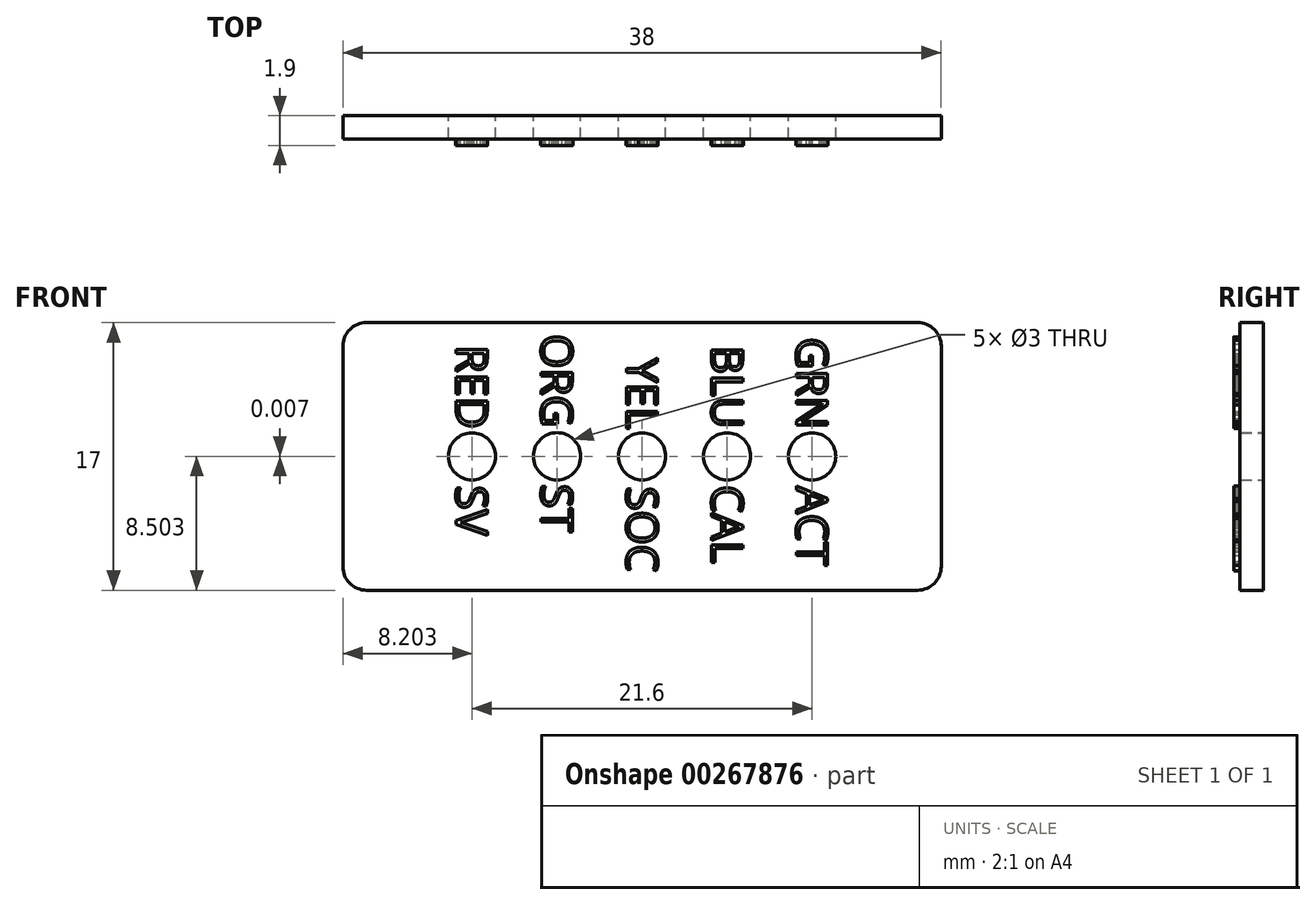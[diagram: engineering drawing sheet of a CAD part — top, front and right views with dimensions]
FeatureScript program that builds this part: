
annotation { "Feature Type Name" : "Feature", "Feature Type Description" : "" }
export const myFeature = defineFeature(function(context is Context, id is Id, definition is map)
    precondition{}
    {
        {
            var Q0;
            Q0=qCreatedBy(makeId("Front.planeOp"),FACE);
            var sketch = newSketch(context, id + "F0", { "sketchPlane" : qUnion([Q0])});
            skLineSegment(sketch, "E0.bottom", {"start": v(-88.73, 33.86) * mm, "end": v(-53.73, 33.86) * mm});
            skLineSegment(sketch, "E0.top", {"start": v(-88.73, 16.86) * mm, "end": v(-53.73, 16.86) * mm});
            skLineSegment(sketch, "E0.left", {"start": v(-90.23, 32.36) * mm, "end": v(-90.23, 18.36) * mm});
            skLineSegment(sketch, "E0.right", {"start": v(-52.23, 32.36) * mm, "end": v(-52.23, 18.36) * mm});
            skLineSegment(sketch, "E1", {"start": v(-94.23, 25.36) * mm, "end": v(-40.36, 25.36) * mm, "construction": true});
            skCircle(sketch, "E2", {"center": v(-82.03, 25.36) * mm, "radius": 1.5 * mm});
            skCircle(sketch, "E3", {"center": v(-76.63, 25.37) * mm, "radius": 1.5 * mm});
            skCircle(sketch, "E4", {"center": v(-71.23, 25.36) * mm, "radius": 1.5 * mm});
            skCircle(sketch, "E5", {"center": v(-65.83, 25.36) * mm, "radius": 1.5 * mm});
            skCircle(sketch, "E6", {"center": v(-60.43, 25.36) * mm, "radius": 1.5 * mm});
            skPoint(sketch, "E7.visualSharp", {"position": v(-90.23, 33.86) * mm});
            skArc(sketch, "E7.filletArc", {"start": v(-88.73, 33.86) * mm, "mid": v(-89.79, 33.42) * mm, "end": v(-90.23, 32.36) * mm});
            skPoint(sketch, "E8.visualSharp", {"position": v(-52.23, 33.86) * mm});
            skArc(sketch, "E8.filletArc", {"start": v(-52.23, 32.36) * mm, "mid": v(-52.67, 33.42) * mm, "end": v(-53.73, 33.86) * mm});
            skPoint(sketch, "E9.visualSharp", {"position": v(-52.23, 16.86) * mm});
            skArc(sketch, "E9.filletArc", {"start": v(-53.73, 16.86) * mm, "mid": v(-52.67, 17.3) * mm, "end": v(-52.23, 18.36) * mm});
            skPoint(sketch, "E10.visualSharp", {"position": v(-90.23, 16.86) * mm});
            skArc(sketch, "E10.filletArc", {"start": v(-90.23, 18.36) * mm, "mid": v(-89.79, 17.3) * mm, "end": v(-88.73, 16.86) * mm});
            skSolve(sketch);
        }
        {
            var Q0;
            Q0=makeQuery(id+"F0.imprint","IMPRINT",FACE,{"disambiguationData":[TD([[makeQuery(id+"F0.imprint","IMPRINT",EDGE,{"derivedFrom":sQuery(id+"F0.wireOp",EDGE,"E0.bottom")}),-1.0]])]});
            extrude(context, id + "F1", {"entities" : qUnion([Q0]), "depth" : 1.5 * mm});
        }
        {
            var Q0;
            Q0=makeQuery(id+"F1.opExtrude","CAP_FACE",FACE,{"disambiguationData":[OSD([sQuery(id+"F0.wireOp",EDGE,"E0.bottom"),sQuery(id+"F0.wireOp",EDGE,"E0.top"),sQuery(id+"F0.wireOp",EDGE,"E0.left"),sQuery(id+"F0.wireOp",EDGE,"E0.right"),sQuery(id+"F0.wireOp",EDGE,"E2"),sQuery(id+"F0.wireOp",EDGE,"E3"),sQuery(id+"F0.wireOp",EDGE,"E4"),sQuery(id+"F0.wireOp",EDGE,"E5"),sQuery(id+"F0.wireOp",EDGE,"E6")])],"isStart":false});
            var sketch = newSketch(context, id + "F2", { "sketchPlane" : qUnion([Q0])});
            skText(sketch, "E11", { "text": "GRN     ACT", "fontName": "OpenSans-Regular.ttf"});
            skText(sketch, "E12", { "text": "BLU     CAL", "fontName": "OpenSans-Regular.ttf"});
            skText(sketch, "E13", { "text": "YEL     SOC", "fontName": "OpenSans-Regular.ttf"});
            skText(sketch, "E14", { "text": "ORG     ST", "fontName": "OpenSans-Regular.ttf"});
            skText(sketch, "E15", { "text": "RED     SV", "fontName": "OpenSans-Regular.ttf"});
            const initialGuessF2  = {"E11": [-0.06143, 0.03291, 0, -1, 0.002], "E12": [-0.06681, 0.0324, 0, -1, 0.002], "E13": [-0.07222, 0.0316, 0, -1, 0.002], "E14": [-0.07764, 0.03312, 0, -1, 0.002], "E15": [-0.08304, 0.03241, 0, -1, 0.002]};
            skSetInitialGuess(sketch, initialGuessF2);
            skSolve(sketch);
        }
        {
            var Q0;
            Q0 = qSketchRegion(id + "F2", true);
            extrude(context, id + "F3", {"entities" : qUnion([Q0]), "operationType" : NewBodyOperationType.ADD, "depth" : 0.4 * mm});
        }
    });
